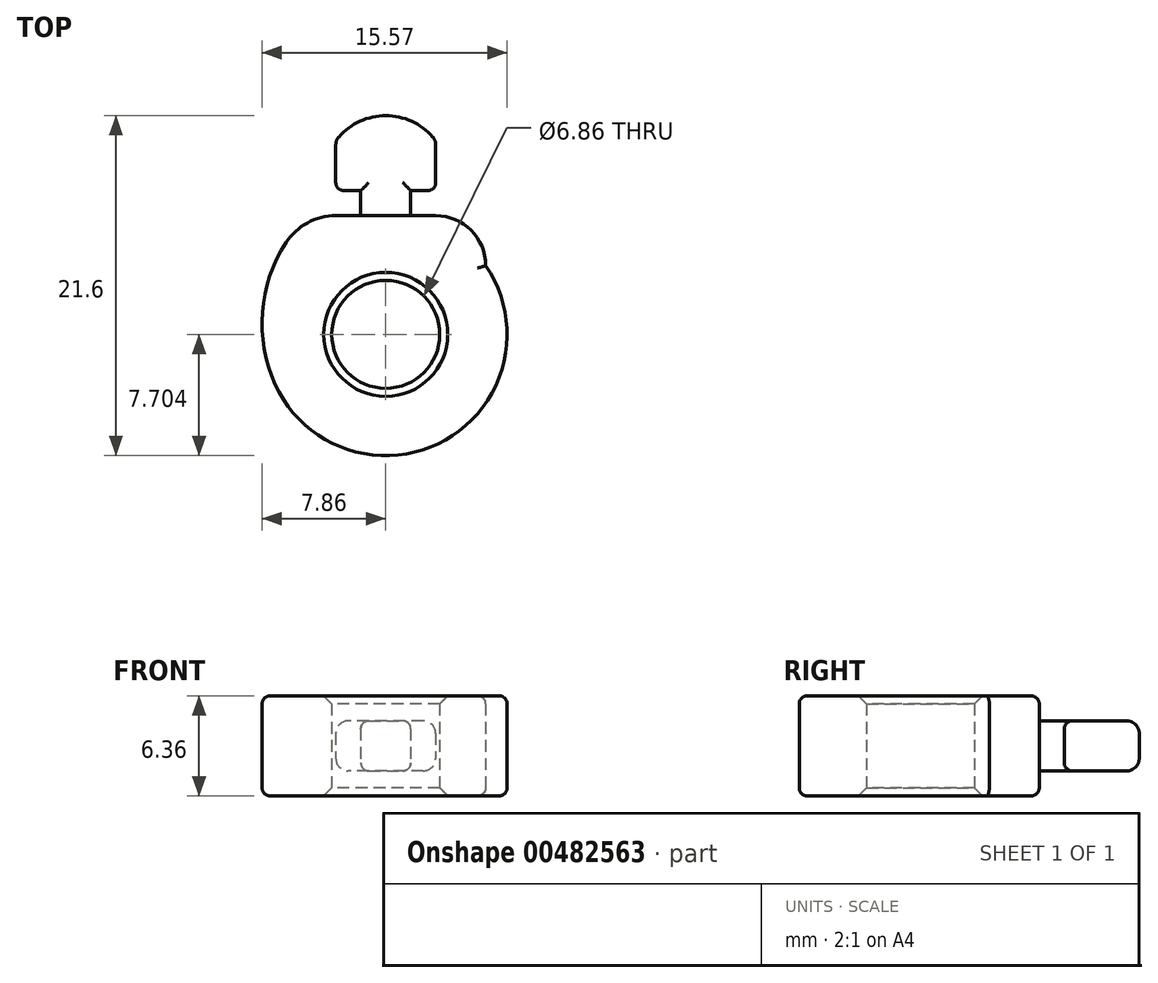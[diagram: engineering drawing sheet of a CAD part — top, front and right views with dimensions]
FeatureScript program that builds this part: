
annotation { "Feature Type Name" : "Feature", "Feature Type Description" : "" }
export const myFeature = defineFeature(function(context is Context, id is Id, definition is map)
    precondition{}
    {
        {
            var Q0;
            Q0=qCreatedBy(makeId("Top.planeOp"),FACE);
            var sketch = newSketch(context, id + "F0", { "sketchPlane" : qUnion([Q0])});
            skLineSegment(sketch, "E0", {"start": v(3.18, 7.94) * mm, "end": v(3.18, 4.76) * mm});
            skLineSegment(sketch, "E1", {"start": v(3.18, 4.76) * mm, "end": v(1.59, 4.76) * mm});
            skLineSegment(sketch, "E2", {"start": v(1.59, 4.76) * mm, "end": v(1.59, 3.17) * mm});
            skLineSegment(sketch, "E3", {"start": v(-1.59, 3.17) * mm, "end": v(-1.59, 4.76) * mm});
            skLineSegment(sketch, "E4", {"start": v(-1.59, 4.76) * mm, "end": v(-3.17, 4.76) * mm});
            skLineSegment(sketch, "E5", {"start": v(-3.17, 4.76) * mm, "end": v(-3.17, 7.94) * mm});
            skLineSegment(sketch, "E6", {"start": v(0, 34.93) * mm, "end": v(0, -21.9) * mm, "construction": true});
            skArc(sketch, "E7", {"start": v(3.18, 7.94) * mm, "mid": v(0, 9.52) * mm, "end": v(-3.17, 7.94) * mm});
            skLineSegment(sketch, "E8", {"start": v(1.59, 3.18) * mm, "end": v(6.35, 3.18) * mm});
            skLineSegment(sketch, "E9", {"start": v(6.35, 3.18) * mm, "end": v(6.35, 0) * mm});
            skLineSegment(sketch, "E10", {"start": v(6.35, 0) * mm, "end": v(-6.35, 0) * mm});
            skLineSegment(sketch, "E11", {"start": v(-6.35, 0) * mm, "end": v(-6.35, 3.17) * mm});
            skLineSegment(sketch, "E12", {"start": v(-6.35, 3.17) * mm, "end": v(-1.59, 3.17) * mm});
            skLineSegment(sketch, "E13", {"start": v(-6.75, 9.52) * mm, "end": v(5.45, 9.52) * mm, "construction": true});
            skLineSegment(sketch, "E14", {"start": v(-1.59, 3.17) * mm, "end": v(1.59, 3.17) * mm});
            skSolve(sketch);
        }
        {
            var Q0;
            Q0=makeQuery(id+"F0.imprint","IMPRINT",FACE,{"disambiguationData":[TD([[makeQuery(id+"F0.imprint","IMPRINT",EDGE,{"derivedFrom":sQuery(id+"F0.wireOp",EDGE,"E0")}),-1.0]])]});
            extrude(context, id + "F1", {"entities" : qUnion([Q0]), "endBound" : BoundingType.SYMMETRIC, "depth" : 3.17 * mm});
        }
        {
            var Q0;
            Q0=makeQuery(id+"F0.imprint","IMPRINT",FACE,{"disambiguationData":[TD([[makeQuery(id+"F0.imprint","IMPRINT",EDGE,{"derivedFrom":sQuery(id+"F0.wireOp",EDGE,"E8")}),-1.0]])]});
            extrude(context, id + "F2", {"entities" : qUnion([Q0]), "operationType" : NewBodyOperationType.ADD, "endBound" : BoundingType.SYMMETRIC, "depth" : 6.35 * mm, "offsetDistance" : 25.4 * mm});
        }
        {
            var Q0;
            Q0=makeQuery(id+"F2.opExtrude","SWEPT_EDGE",EDGE,{"disambiguationData":[OSD([sQuery(id+"F0.wireOp",EDGE,"E8"),sQuery(id+"F0.wireOp",EDGE,"E9")])]});
            var Q1;
            Q1=makeQuery(id+"F2.opExtrude","SWEPT_EDGE",EDGE,{"disambiguationData":[OSD([sQuery(id+"F0.wireOp",EDGE,"E11"),sQuery(id+"F0.wireOp",EDGE,"E12")])]});
            fillet(context, id + "F3", {"entities" : qUnion([Q0, Q1]), "radius" : 3.17 * mm, "tangentPropagation" : true, "allowEdgeOverflow" : false});
        }
        {
            var Q0;
            Q0=makeQuery(id+"F1.opExtrude","CAP_EDGE",EDGE,{"disambiguationData":[OSD([sQuery(id+"F0.wireOp",EDGE,"E7")])],"isStart":true});
            var Q1;
            Q1=makeQuery(id+"F1.opExtrude","CAP_EDGE",EDGE,{"disambiguationData":[OSD([sQuery(id+"F0.wireOp",EDGE,"E7")])],"isStart":false});
            var Q2;
            Q2=makeQuery(id+"F1.opExtrude","CAP_EDGE",EDGE,{"disambiguationData":[OSD([sQuery(id+"F0.wireOp",EDGE,"E0")])],"isStart":true});
            var Q3;
            Q3=makeQuery(id+"F1.opExtrude","CAP_EDGE",EDGE,{"disambiguationData":[OSD([sQuery(id+"F0.wireOp",EDGE,"E0")])],"isStart":false});
            var Q4;
            Q4=makeQuery(id+"F1.opExtrude","CAP_EDGE",EDGE,{"disambiguationData":[OSD([sQuery(id+"F0.wireOp",EDGE,"E5")])],"isStart":true});
            var Q5;
            Q5=makeQuery(id+"F1.opExtrude","CAP_EDGE",EDGE,{"disambiguationData":[OSD([sQuery(id+"F0.wireOp",EDGE,"E5")])],"isStart":false});
            var Q6;
            Q6=makeQuery(id+"F1.opExtrude","SWEPT_EDGE",EDGE,{"disambiguationData":[OSD([sQuery(id+"F0.wireOp",EDGE,"E0"),sQuery(id+"F0.wireOp",EDGE,"E7")])]});
            var Q7;
            Q7=makeQuery(id+"F1.opExtrude","SWEPT_EDGE",EDGE,{"disambiguationData":[OSD([sQuery(id+"F0.wireOp",EDGE,"E5"),sQuery(id+"F0.wireOp",EDGE,"E7")])]});
            fillet(context, id + "F4", {"entities" : qUnion([Q0, Q1, Q2, Q3, Q4, Q5, Q6, Q7]), "radius" : 0.8 * mm, "tangentPropagation" : true, "allowEdgeOverflow" : false});
        }
        {
            var Q0;
            Q0=qCreatedBy(makeId("Top.planeOp"),FACE);
            var sketch = newSketch(context, id + "F5", { "sketchPlane" : qUnion([Q0])});
            skArc(sketch, "E15", {"start": v(7.02, -7.54) * mm, "mid": v(6.87, -0.88) * mm, "end": v(1.59, 3.18) * mm, "construction": true});
            skArc(sketch, "E16", {"start": v(0, -7.8) * mm, "mid": v(3.43, -4.37) * mm, "end": v(0, -0.94) * mm});
            skLineSegment(sketch, "E17", {"start": v(0, 18.67) * mm, "end": v(0, -29.68) * mm, "construction": true});
            skArc(sketch, "E18.MirrorCS", {"start": v(0, -7.8) * mm, "mid": v(-3.43, -4.37) * mm, "end": v(0, -0.94) * mm});
            skPoint(sketch, "E19.0", {"position": v(-3.18, 3.17) * mm});
            skPoint(sketch, "E20.0", {"position": v(3.17, 3.17) * mm});
            skArc(sketch, "E21", {"start": v(-3.18, 3.17) * mm, "mid": v(-4.97, 2.72) * mm, "end": v(-6.34, 1.46) * mm});
            skArc(sketch, "E22", {"start": v(-6.34, 1.46) * mm, "mid": v(-7.83, -2.95) * mm, "end": v(-7.02, -7.54) * mm});
            skPoint(sketch, "E23.MirrorCS.end.orphan", {"position": v(0, 3.34) * mm});
            skArc(sketch, "E24.MirrorCS", {"start": v(6.34, 1.46) * mm, "mid": v(7.83, -2.95) * mm, "end": v(7.02, -7.54) * mm});
            skArc(sketch, "E25.MirrorCS", {"start": v(3.18, 3.17) * mm, "mid": v(4.97, 2.72) * mm, "end": v(6.34, 1.46) * mm});
            skArc(sketch, "E26", {"start": v(-1.59, 3.17) * mm, "mid": v(-6.87, -0.88) * mm, "end": v(-7.02, -7.54) * mm, "construction": true});
            skLineSegment(sketch, "E27", {"start": v(-3.18, 3.17) * mm, "end": v(3.17, 3.17) * mm});
            skArc(sketch, "E28", {"start": v(-1.59, 3.17) * mm, "mid": v(0, -12.07) * mm, "end": v(1.59, 3.17) * mm});
            skSolve(sketch);
        }
        {
            var Q0;
            {var subQ0=sQuery(id+"F5.wireOp",EDGE,"E28");var subQ2=sQuery(id+"F5.wireOp",EDGE,"E27");var subQ5=makeQuery(id+"F5.imprint","INTERSECT",VERTEX,{"disambiguationData":[OD(0.0)],"derivedFrom":[subQ2,subQ0]});Q0=makeQuery(id+"F5.imprint","IMPRINT",FACE,{"disambiguationData":[TD([[makeQuery(id+"F5.imprint","IMPRINT",EDGE,{"disambiguationData":[TD([[subQ5,-1.0]])],"derivedFrom":subQ2}),-1.0]])]});}
            var Q1;
            {var subQ0=sQuery(id+"F5.wireOp",EDGE,"E24.MirrorCS");Q1=makeQuery(id+"F5.imprint","IMPRINT",FACE,{"disambiguationData":[TD([[makeQuery(id+"F5.imprint","IMPRINT",EDGE,{"derivedFrom":subQ0}),-1.0]])]});}
            var Q2;
            {var subQ0=sQuery(id+"F5.wireOp",EDGE,"E21");Q2=makeQuery(id+"F5.imprint","IMPRINT",FACE,{"disambiguationData":[TD([[makeQuery(id+"F5.imprint","IMPRINT",EDGE,{"derivedFrom":subQ0}),1.0]])]});}
            extrude(context, id + "F6", {"entities" : qUnion([Q0, Q1, Q2]), "operationType" : NewBodyOperationType.ADD, "endBound" : BoundingType.SYMMETRIC, "depth" : 6.35 * mm, "offsetDistance" : 25.4 * mm});
        }
        {
            var Q0;
            Q0=makeQuery(id+"F1.opExtrude","CAP_EDGE",EDGE,{"disambiguationData":[OSD([sQuery(id+"F0.wireOp",EDGE,"E14")])],"isStart":true});
            var Q1;
            Q1=makeQuery(id+"F1.opExtrude","SWEPT_EDGE",EDGE,{"disambiguationData":[OSD([sQuery(id+"F0.wireOp",EDGE,"E3"),sQuery(id+"F0.wireOp",EDGE,"E12"),sQuery(id+"F0.wireOp",EDGE,"E14")])]});
            var Q2;
            Q2=makeQuery(id+"F1.opExtrude","CAP_EDGE",EDGE,{"disambiguationData":[OSD([sQuery(id+"F0.wireOp",EDGE,"E14")])],"isStart":false});
            var Q3;
            Q3=makeQuery(id+"F1.opExtrude","SWEPT_EDGE",EDGE,{"disambiguationData":[OSD([sQuery(id+"F0.wireOp",EDGE,"E2"),sQuery(id+"F0.wireOp",EDGE,"E8"),sQuery(id+"F0.wireOp",EDGE,"E14")])]});
            var Q4;
            Q4=makeQuery(id+"F1.opExtrude","CAP_EDGE",EDGE,{"disambiguationData":[OSD([sQuery(id+"F0.wireOp",EDGE,"E2")])],"isStart":false});
            var Q5;
            Q5=makeQuery(id+"F1.opExtrude","CAP_EDGE",EDGE,{"disambiguationData":[OSD([sQuery(id+"F0.wireOp",EDGE,"E2")])],"isStart":true});
            var Q6;
            Q6=makeQuery(id+"F1.opExtrude","CAP_EDGE",EDGE,{"disambiguationData":[OSD([sQuery(id+"F0.wireOp",EDGE,"E3")])],"isStart":true});
            var Q7;
            Q7=makeQuery(id+"F1.opExtrude","CAP_EDGE",EDGE,{"disambiguationData":[OSD([sQuery(id+"F0.wireOp",EDGE,"E3")])],"isStart":false});
            var Q8;
            Q8=makeQuery(id+"F4.opFillet","BLEND_EDGE",EDGE,{"blendedFrom":[makeQuery(id+"F1.opExtrude","CAP_EDGE",EDGE,{"disambiguationData":[OSD([sQuery(id+"F0.wireOp",EDGE,"E0")])],"isStart":false}),makeQuery(id+"F1.opExtrude","SWEPT_FACE",FACE,{"disambiguationData":[OSD([sQuery(id+"F0.wireOp",EDGE,"E1")])]})],"blendedInto":[makeQuery(id+"F1.opExtrude","SWEPT_FACE",FACE,{"disambiguationData":[OSD([sQuery(id+"F0.wireOp",EDGE,"E1")])]})]});
            var Q9;
            Q9=makeQuery(id+"F4.opFillet","BLEND_EDGE",EDGE,{"blendedFrom":[makeQuery(id+"F1.opExtrude","CAP_EDGE",EDGE,{"disambiguationData":[OSD([sQuery(id+"F0.wireOp",EDGE,"E5")])],"isStart":true}),makeQuery(id+"F1.opExtrude","SWEPT_FACE",FACE,{"disambiguationData":[OSD([sQuery(id+"F0.wireOp",EDGE,"E4")])]})],"blendedInto":[makeQuery(id+"F1.opExtrude","SWEPT_FACE",FACE,{"disambiguationData":[OSD([sQuery(id+"F0.wireOp",EDGE,"E4")])]})]});
            fillet(context, id + "F7", {"entities" : qUnion([Q0, Q1, Q2, Q3, Q4, Q5, Q6, Q7, Q8, Q9]), "radius" : 0.5 * mm, "tangentPropagation" : true, "allowEdgeOverflow" : false});
        }
        {
            var Q0;
            Q0=makeQuery(id+"F6.opExtrude","CAP_EDGE",EDGE,{"disambiguationData":[OSD([sQuery(id+"F5.wireOp",EDGE,"E22")])],"isStart":true});
            var Q1;
            Q1=makeQuery(id+"F6.opExtrude","CAP_EDGE",EDGE,{"disambiguationData":[OSD([sQuery(id+"F5.wireOp",EDGE,"E22")])],"isStart":false});
            var Q2;
            {var subQ1=sQuery(id+"F5.wireOp",EDGE,"08AbskoX-ZJT4-CmZR-Mk2I-tWpXKzvuXNzW");var subQ2=sQuery(id+"F5.wireOp",EDGE,"PTXDY87q-BvN2-vXKg-RxmP-ChUVbQPWyHip");Q2=makeQuery(id+"FRWU9TcJ6aRfyBu_3.boolean.opBoolean","SPLIT",FACE,{"disambiguationData":[TD([makeQuery(id+"FRWU9TcJ6aRfyBu_3.opPattern","COPY",FACE,{"derivedFrom":makeQuery(id+"F77W5iahoIH3pZr_2.opExtrude","SWEPT_FACE",FACE,{"disambiguationData":[OSD([subQ2])]}),"instanceName":"1"})])],"derivedFrom":makeQuery(id+"F6.opExtrude","SWEPT_FACE",FACE,{"disambiguationData":[OSD([subQ1])]})});}
            var Q3;
            {var subQ0=sQuery(id+"F5.wireOp",EDGE,"PTXDY87q-BvN2-vXKg-RxmP-ChUVbQPWyHip");var subQ2=sQuery(id+"F5.wireOp",EDGE,"08AbskoX-ZJT4-CmZR-Mk2I-tWpXKzvuXNzW");Q3=makeQuery(id+"FRWU9TcJ6aRfyBu_3.boolean.opBoolean","SPLIT",FACE,{"disambiguationData":[TD([makeQuery(id+"F77W5iahoIH3pZr_2.opExtrude","SWEPT_FACE",FACE,{"disambiguationData":[OSD([subQ0])]})])],"derivedFrom":makeQuery(id+"F6.opExtrude","SWEPT_FACE",FACE,{"disambiguationData":[OSD([subQ2])]})});}
            var Q4;
            {var subQ0=sQuery(id+"F5.wireOp",EDGE,"J4r9OVjn-GWRR-N2AY-Khi5-idb3etWEovZE");var subQ3=sQuery(id+"F5.wireOp",EDGE,"17ckoiND-pfTU-ipib-qScu-VgyzAWnOci4f");Q4=makeQuery(id+"FRWU9TcJ6aRfyBu_3.boolean.opBoolean","SPLIT",FACE,{"disambiguationData":[TD([makeQuery(id+"F77W5iahoIH3pZr_2.opExtrude","SWEPT_FACE",FACE,{"disambiguationData":[OSD([subQ3])]})])],"derivedFrom":makeQuery(id+"FDtQxmCBpzsJdCM_1.opExtrude","SWEPT_FACE",FACE,{"disambiguationData":[OSD([subQ0])]})});}
            var Q5;
            {var subQ0=sQuery(id+"F5.wireOp",EDGE,"J4r9OVjn-GWRR-N2AY-Khi5-idb3etWEovZE");var subQ2=sQuery(id+"F5.wireOp",EDGE,"PTXDY87q-BvN2-vXKg-RxmP-ChUVbQPWyHip");Q5=makeQuery(id+"FRWU9TcJ6aRfyBu_3.boolean.opBoolean","SPLIT",FACE,{"disambiguationData":[TD([makeQuery(id+"FRWU9TcJ6aRfyBu_3.opPattern","COPY",FACE,{"derivedFrom":makeQuery(id+"F77W5iahoIH3pZr_2.opExtrude","SWEPT_FACE",FACE,{"disambiguationData":[OSD([subQ2])]}),"instanceName":"1"})])],"derivedFrom":makeQuery(id+"FDtQxmCBpzsJdCM_1.opExtrude","SWEPT_FACE",FACE,{"disambiguationData":[OSD([subQ0])]})});}
            var Q6;
            {var subQ0=sQuery(id+"F5.wireOp",EDGE,"PTXDY87q-BvN2-vXKg-RxmP-ChUVbQPWyHip");var subQ1=sQuery(id+"F5.wireOp",EDGE,"J4r9OVjn-GWRR-N2AY-Khi5-idb3etWEovZE");Q6=makeQuery(id+"FRWU9TcJ6aRfyBu_3.boolean.opBoolean","SPLIT",FACE,{"disambiguationData":[TD([makeQuery(id+"F77W5iahoIH3pZr_2.opExtrude","SWEPT_FACE",FACE,{"disambiguationData":[OSD([subQ0])]})])],"derivedFrom":makeQuery(id+"FDtQxmCBpzsJdCM_1.opExtrude","SWEPT_FACE",FACE,{"disambiguationData":[OSD([subQ1])]})});}
            var Q7;
            {var subQ1=sQuery(id+"F5.wireOp",EDGE,"08AbskoX-ZJT4-CmZR-Mk2I-tWpXKzvuXNzW");var subQ3=sQuery(id+"F5.wireOp",EDGE,"17ckoiND-pfTU-ipib-qScu-VgyzAWnOci4f");Q7=makeQuery(id+"FRWU9TcJ6aRfyBu_3.boolean.opBoolean","SPLIT",FACE,{"disambiguationData":[TD([makeQuery(id+"F77W5iahoIH3pZr_2.opExtrude","SWEPT_FACE",FACE,{"disambiguationData":[OSD([subQ3])]})])],"derivedFrom":makeQuery(id+"F6.opExtrude","SWEPT_FACE",FACE,{"disambiguationData":[OSD([subQ1])]})});}
            fillet(context, id + "F8", {"entities" : qUnion([Q0, Q1, Q2, Q3, Q4, Q5, Q6, Q7]), "radius" : 0.5 * mm, "tangentPropagation" : true, "allowEdgeOverflow" : false});
        }
        {
            var Q0;
            Q0=makeQuery(id+"F6.opExtrude","CAP_EDGE",EDGE,{"disambiguationData":[OSD([sQuery(id+"F5.wireOp",EDGE,"E16"),sQuery(id+"F5.wireOp",EDGE,"E18.MirrorCS")])],"isStart":false});
            var Q1;
            Q1=makeQuery(id+"F6.opExtrude","CAP_EDGE",EDGE,{"disambiguationData":[OSD([sQuery(id+"F5.wireOp",EDGE,"E16"),sQuery(id+"F5.wireOp",EDGE,"E18.MirrorCS")])],"isStart":true});
            chamfer(context, id + "F9", {"entities" : qUnion([Q0, Q1]), "width" : 0.5 * mm, "tangentPropagation" : true});
        }
    });
